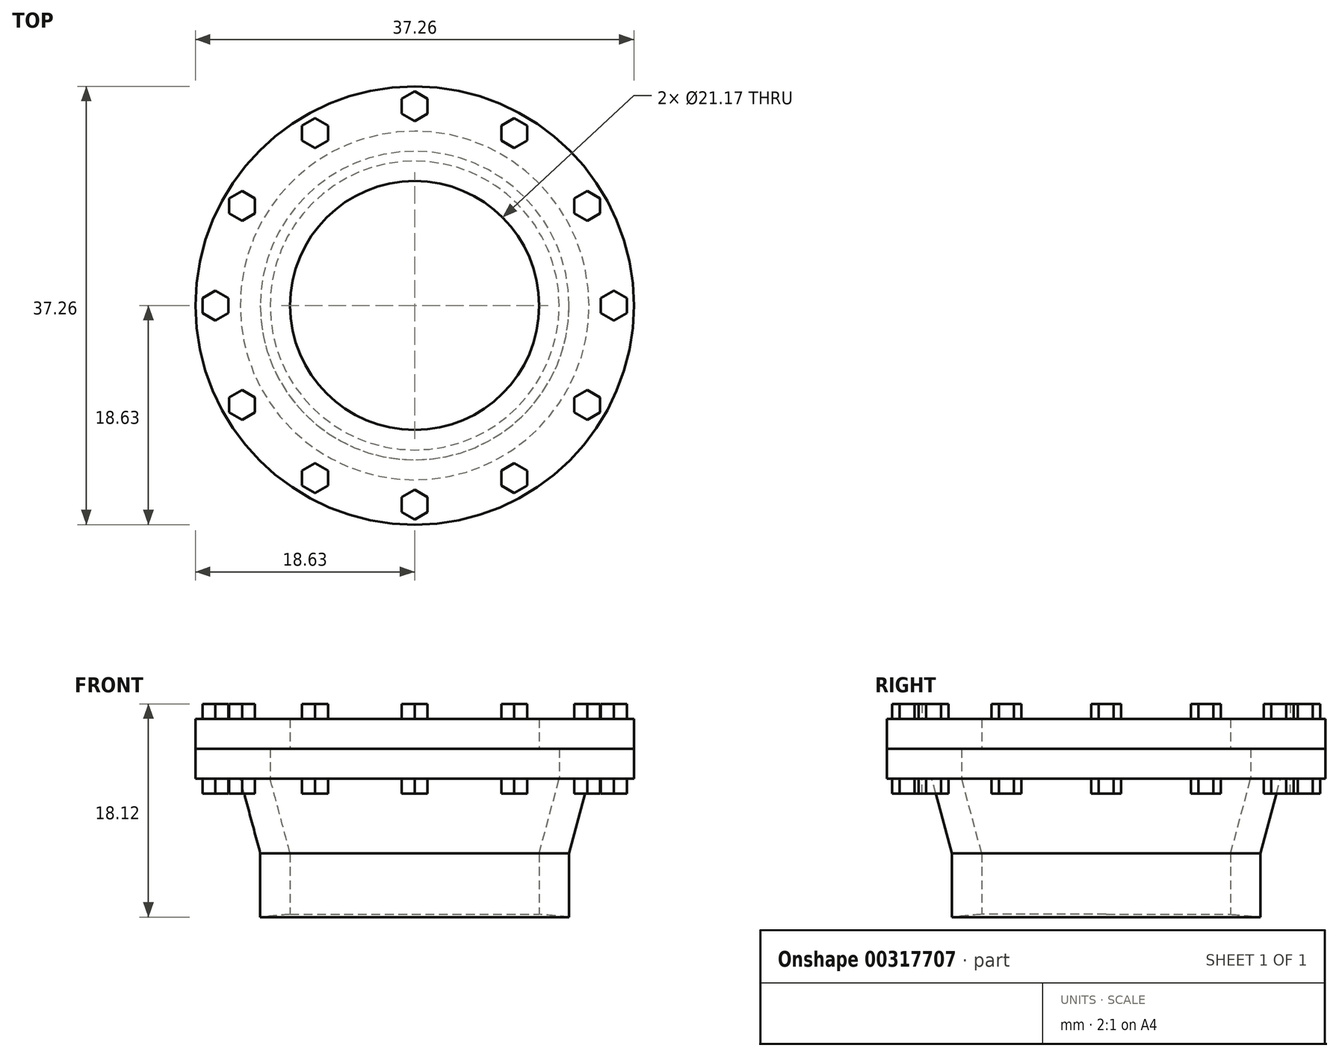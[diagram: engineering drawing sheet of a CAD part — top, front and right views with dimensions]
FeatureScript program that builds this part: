
annotation { "Feature Type Name" : "Feature", "Feature Type Description" : "" }
export const myFeature = defineFeature(function(context is Context, id is Id, definition is map)
    precondition{}
    {
        {
            var Q0;
            Q0=qCreatedBy(makeId("Front.planeOp"),FACE);
            var sketch = newSketch(context, id + "F0", { "sketchPlane" : qUnion([Q0])});
            skLineSegment(sketch, "E0", {"start": v(0, 0) * mm, "end": v(66.68, 0) * mm, "construction": true});
            skLineSegment(sketch, "E1", {"start": v(0, 0) * mm, "end": v(0, 33.34) * mm, "construction": true});
            skLineSegment(sketch, "E2", {"start": v(0, 33.34) * mm, "end": v(0, 36.51) * mm});
            skLineSegment(sketch, "E3", {"start": v(66.68, 0) * mm, "end": v(69.85, 0) * mm});
            skEllipse(sketch, "E4", {"center": v(0, 0) * mm, "majorRadius": 66.68 * mm, "minorRadius": 33.34 * mm, "majorAxis": v(1, 0)});
            skEllipse(sketch, "E5", {"center": v(0, 0) * mm, "majorRadius": 69.85 * mm, "minorRadius": 36.51 * mm, "majorAxis": v(1, 0)});
            skSolve(sketch);
        }
        {
            var Q0;
            {var subQ0=sQuery(id+"F0.wireOp",EDGE,"E2");Q0=makeQuery(id+"F0.imprint","IMPRINT",FACE,{"disambiguationData":[TD([[makeQuery(id+"F0.imprint","IMPRINT",EDGE,{"derivedFrom":subQ0}),-1.0]])]});}
            var Q1;
            Q1=sQuery(id+"F0.wireOp",EDGE,"E1");
            revolve(context, id + "F1", {"entities" : qUnion([Q0]), "axis" : qUnion([Q1]), "revolveType" : RevolveType.FULL});
        }
        {
            var Q0;
            Q0=qCreatedBy(makeId("Front.planeOp"),FACE);
            var sketch = newSketch(context, id + "F2", { "sketchPlane" : qUnion([Q0])});
            skLineSegment(sketch, "E6", {"start": v(0, 0) * mm, "end": v(0, 34.93) * mm, "construction": true});
            skLineSegment(sketch, "E7", {"start": v(-10.58, 34.93) * mm, "end": v(10.58, 34.93) * mm, "construction": true});
            skLineSegment(sketch, "E8", {"start": v(-10.58, 34.93) * mm, "end": v(-10.58, 33.02) * mm});
            skLineSegment(sketch, "E9", {"start": v(-10.58, 34.93) * mm, "end": v(-10.58, 41.27) * mm});
            skLineSegment(sketch, "E10", {"start": v(10.58, 34.93) * mm, "end": v(10.58, 33.02) * mm});
            skLineSegment(sketch, "E11", {"start": v(10.58, 34.93) * mm, "end": v(10.58, 41.27) * mm});
            skLineSegment(sketch, "E12.bottom", {"start": v(-10.58, 41.27) * mm, "end": v(-13.12, 41.27) * mm});
            skLineSegment(sketch, "E12.top", {"start": v(-10.58, 33.02) * mm, "end": v(-13.12, 33.02) * mm});
            skLineSegment(sketch, "E12.left", {"start": v(-10.58, 41.27) * mm, "end": v(-10.58, 33.02) * mm});
            skLineSegment(sketch, "E12.right", {"start": v(-13.12, 41.27) * mm, "end": v(-13.12, 33.02) * mm});
            skLineSegment(sketch, "E13", {"start": v(-13.12, 41.27) * mm, "end": v(-14.82, 47.62) * mm});
            skLineSegment(sketch, "E14", {"start": v(-14.82, 47.62) * mm, "end": v(-12.28, 47.62) * mm});
            skLineSegment(sketch, "E15", {"start": v(-12.28, 47.62) * mm, "end": v(-10.58, 41.27) * mm});
            skLineSegment(sketch, "E16.bottom", {"start": v(-12.28, 47.62) * mm, "end": v(-18.63, 47.62) * mm});
            skLineSegment(sketch, "E16.top", {"start": v(-12.28, 50.16) * mm, "end": v(-18.63, 50.16) * mm});
            skLineSegment(sketch, "E16.left", {"start": v(-12.28, 47.62) * mm, "end": v(-12.28, 50.17) * mm});
            skLineSegment(sketch, "E16.right", {"start": v(-18.63, 47.62) * mm, "end": v(-18.63, 50.16) * mm});
            skLineSegment(sketch, "E17", {"start": v(0, 34.93) * mm, "end": v(0, 57.33) * mm, "construction": true});
            skLineSegment(sketch, "E18.bottom", {"start": v(-12.28, 47.62) * mm, "end": v(0, 47.62) * mm});
            skLineSegment(sketch, "E18.top", {"start": v(-12.28, 50.17) * mm, "end": v(0, 50.17) * mm});
            skLineSegment(sketch, "E18.right", {"start": v(0, 47.62) * mm, "end": v(0, 50.17) * mm});
            skLineSegment(sketch, "E19.bottom", {"start": v(-18.63, 50.16) * mm, "end": v(0, 50.16) * mm});
            skLineSegment(sketch, "E19.top", {"start": v(-18.63, 52.7) * mm, "end": v(0, 52.7) * mm});
            skLineSegment(sketch, "E19.left", {"start": v(-18.63, 50.16) * mm, "end": v(-18.63, 52.7) * mm});
            skLineSegment(sketch, "E19.right", {"start": v(0, 50.17) * mm, "end": v(0, 52.7) * mm});
            skSolve(sketch);
        }
        {
            var Q0;
            Q0=makeQuery(id+"F2.imprint","IMPRINT",FACE,{"disambiguationData":[TD([[makeQuery(id+"F2.imprint","IMPRINT",EDGE,{"derivedFrom":sQuery(id+"F2.wireOp",EDGE,"E12.bottom")}),1.0]])]});
            var Q1;
            Q1=makeQuery(id+"F2.imprint","IMPRINT",FACE,{"disambiguationData":[TD([[makeQuery(id+"F2.imprint","IMPRINT",EDGE,{"derivedFrom":sQuery(id+"F2.wireOp",EDGE,"E12.bottom")}),-1.0]])]});
            var Q2;
            Q2=makeQuery(id+"F2.imprint","IMPRINT",FACE,{"disambiguationData":[TD([[makeQuery(id+"F2.imprint","IMPRINT",EDGE,{"derivedFrom":sQuery(id+"F2.wireOp",EDGE,"E16.top")}),1.0]])]});
            var Q3;
            {var subQ1=sQuery(id+"F2.wireOp",EDGE,"E16.right");Q3=makeQuery(id+"F2.imprint","IMPRINT",FACE,{"disambiguationData":[TD([[makeQuery(id+"F2.imprint","IMPRINT",EDGE,{"derivedFrom":subQ1}),-1.0]])]});}
            var Q4;
            Q4=sQuery(id+"F2.wireOp",EDGE,"E17");
            revolve(context, id + "F3", {"entities" : qUnion([Q0, Q1, Q2, Q3]), "axis" : qUnion([Q4]), "revolveType" : RevolveType.FULL});
        }
        {
            var Q0;
            Q0=makeQuery(id+"F2.imprint","IMPRINT",FACE,{"disambiguationData":[TD([[makeQuery(id+"F2.imprint","IMPRINT",EDGE,{"derivedFrom":sQuery(id+"F2.wireOp",EDGE,"E19.top")}),-1.0]])]});
            var Q1;
            Q1=sQuery(id+"F2.wireOp",EDGE,"E17");
            revolve(context, id + "F4", {"entities" : qUnion([Q0]), "axis" : qUnion([Q1]), "revolveType" : RevolveType.FULL});
        }
        {
            var Q0;
            Q0=makeQuery(id+"F4.opRevolve","SWEPT_FACE",FACE,{"disambiguationData":[OSD([sQuery(id+"F2.wireOp",EDGE,"E19.top")])]});
            var sketch = newSketch(context, id + "F5", { "sketchPlane" : qUnion([Q0])});
            skLineSegment(sketch, "E20", {"start": v(0, 0) * mm, "end": v(0, -16.93) * mm, "construction": true});
            skLineSegment(sketch, "E21", {"start": v(0, 0) * mm, "end": v(-16.93, 0) * mm, "construction": true});
            skLineSegment(sketch, "E22", {"start": v(0, 0) * mm, "end": v(0, 16.93) * mm, "construction": true});
            skLineSegment(sketch, "E23", {"start": v(0, 0) * mm, "end": v(16.93, 0) * mm, "construction": true});
            skLineSegment(sketch, "E24", {"start": v(0, 0) * mm, "end": v(8.47, 14.66) * mm, "construction": true});
            skLineSegment(sketch, "E25", {"start": v(0, 0) * mm, "end": v(14.66, 8.47) * mm, "construction": true});
            skLineSegment(sketch, "E26", {"start": v(0, 0) * mm, "end": v(14.66, -8.47) * mm, "construction": true});
            skLineSegment(sketch, "E27", {"start": v(0, 0) * mm, "end": v(8.47, -14.66) * mm, "construction": true});
            skLineSegment(sketch, "E28", {"start": v(0, 0) * mm, "end": v(-8.47, -14.66) * mm, "construction": true});
            skLineSegment(sketch, "E29", {"start": v(0, 0) * mm, "end": v(-14.66, -8.47) * mm, "construction": true});
            skLineSegment(sketch, "E30", {"start": v(0, 0) * mm, "end": v(-14.66, 8.47) * mm, "construction": true});
            skLineSegment(sketch, "E31", {"start": v(0, 0) * mm, "end": v(-8.47, 14.66) * mm, "construction": true});
            skCircle(sketch, "E32.cCircle", {"center": v(0, 16.93) * mm, "radius": 1.1 * mm, "construction": true});
            skLineSegment(sketch, "E32.0", {"start": v(1.1, 17.57) * mm, "end": v(1.1, 16.3) * mm});
            skLineSegment(sketch, "E32.1", {"start": v(1.1, 16.3) * mm, "end": v(0, 15.66) * mm});
            skLineSegment(sketch, "E32.2", {"start": v(0, 15.66) * mm, "end": v(-1.1, 16.3) * mm});
            skLineSegment(sketch, "E32.3", {"start": v(-1.1, 16.3) * mm, "end": v(-1.1, 17.57) * mm});
            skLineSegment(sketch, "E32.4", {"start": v(-1.1, 17.57) * mm, "end": v(0, 18.2) * mm});
            skLineSegment(sketch, "E32.5", {"start": v(0, 18.2) * mm, "end": v(1.1, 17.57) * mm});
            skPoint(sketch, "E32.0.midPoint", {"position": v(1.1, 16.93) * mm});
            skCircle(sketch, "E33.cCircle", {"center": v(8.47, 14.66) * mm, "radius": 1.1 * mm, "construction": true});
            skLineSegment(sketch, "E33.0", {"start": v(9.57, 15.3) * mm, "end": v(9.57, 14.03) * mm});
            skLineSegment(sketch, "E33.1", {"start": v(9.57, 14.03) * mm, "end": v(8.47, 13.4) * mm});
            skLineSegment(sketch, "E33.2", {"start": v(8.47, 13.4) * mm, "end": v(7.37, 14.03) * mm});
            skLineSegment(sketch, "E33.3", {"start": v(7.37, 14.03) * mm, "end": v(7.37, 15.3) * mm});
            skLineSegment(sketch, "E33.4", {"start": v(7.37, 15.3) * mm, "end": v(8.47, 15.93) * mm});
            skLineSegment(sketch, "E33.5", {"start": v(8.47, 15.93) * mm, "end": v(9.57, 15.3) * mm});
            skPoint(sketch, "E33.0.midPoint", {"position": v(9.57, 14.66) * mm});
            skCircle(sketch, "E34.cCircle", {"center": v(14.66, 8.47) * mm, "radius": 1.1 * mm, "construction": true});
            skLineSegment(sketch, "E34.0", {"start": v(15.76, 9.1) * mm, "end": v(15.76, 7.83) * mm});
            skLineSegment(sketch, "E34.1", {"start": v(15.76, 7.83) * mm, "end": v(14.66, 7.2) * mm});
            skLineSegment(sketch, "E34.2", {"start": v(14.66, 7.2) * mm, "end": v(13.56, 7.83) * mm});
            skLineSegment(sketch, "E34.3", {"start": v(13.56, 7.83) * mm, "end": v(13.56, 9.1) * mm});
            skLineSegment(sketch, "E34.4", {"start": v(13.56, 9.1) * mm, "end": v(14.66, 9.74) * mm});
            skLineSegment(sketch, "E34.5", {"start": v(14.66, 9.74) * mm, "end": v(15.76, 9.1) * mm});
            skPoint(sketch, "E34.0.midPoint", {"position": v(15.76, 8.47) * mm});
            skCircle(sketch, "E35.cCircle", {"center": v(16.93, 0) * mm, "radius": 1.1 * mm, "construction": true});
            skLineSegment(sketch, "E35.0", {"start": v(18.03, 0.64) * mm, "end": v(18.03, -0.64) * mm});
            skLineSegment(sketch, "E35.1", {"start": v(18.03, -0.64) * mm, "end": v(16.93, -1.27) * mm});
            skLineSegment(sketch, "E35.2", {"start": v(16.93, -1.27) * mm, "end": v(15.83, -0.64) * mm});
            skLineSegment(sketch, "E35.3", {"start": v(15.83, -0.64) * mm, "end": v(15.83, 0.64) * mm});
            skLineSegment(sketch, "E35.4", {"start": v(15.83, 0.64) * mm, "end": v(16.93, 1.27) * mm});
            skLineSegment(sketch, "E35.5", {"start": v(16.93, 1.27) * mm, "end": v(18.03, 0.64) * mm});
            skPoint(sketch, "E35.0.midPoint", {"position": v(18.03, 0) * mm});
            skCircle(sketch, "E36.cCircle", {"center": v(14.66, -8.47) * mm, "radius": 1.1 * mm, "construction": true});
            skLineSegment(sketch, "E36.0", {"start": v(15.76, -7.83) * mm, "end": v(15.76, -9.1) * mm});
            skLineSegment(sketch, "E36.1", {"start": v(15.76, -9.1) * mm, "end": v(14.66, -9.74) * mm});
            skLineSegment(sketch, "E36.2", {"start": v(14.66, -9.74) * mm, "end": v(13.56, -9.1) * mm});
            skLineSegment(sketch, "E36.3", {"start": v(13.56, -9.1) * mm, "end": v(13.56, -7.83) * mm});
            skLineSegment(sketch, "E36.4", {"start": v(13.56, -7.83) * mm, "end": v(14.66, -7.2) * mm});
            skLineSegment(sketch, "E36.5", {"start": v(14.66, -7.2) * mm, "end": v(15.76, -7.83) * mm});
            skPoint(sketch, "E36.0.midPoint", {"position": v(15.76, -8.47) * mm});
            skCircle(sketch, "E37.cCircle", {"center": v(8.47, -14.66) * mm, "radius": 1.1 * mm, "construction": true});
            skLineSegment(sketch, "E37.0", {"start": v(9.57, -14.03) * mm, "end": v(9.57, -15.3) * mm});
            skLineSegment(sketch, "E37.1", {"start": v(9.57, -15.3) * mm, "end": v(8.47, -15.93) * mm});
            skLineSegment(sketch, "E37.2", {"start": v(8.47, -15.93) * mm, "end": v(7.37, -15.3) * mm});
            skLineSegment(sketch, "E37.3", {"start": v(7.37, -15.3) * mm, "end": v(7.37, -14.03) * mm});
            skLineSegment(sketch, "E37.4", {"start": v(7.37, -14.03) * mm, "end": v(8.47, -13.4) * mm});
            skLineSegment(sketch, "E37.5", {"start": v(8.47, -13.4) * mm, "end": v(9.57, -14.03) * mm});
            skPoint(sketch, "E37.0.midPoint", {"position": v(9.57, -14.66) * mm});
            skCircle(sketch, "E38.cCircle", {"center": v(0, -16.93) * mm, "radius": 1.1 * mm, "construction": true});
            skLineSegment(sketch, "E38.0", {"start": v(1.1, -16.3) * mm, "end": v(1.1, -17.57) * mm});
            skLineSegment(sketch, "E38.1", {"start": v(1.1, -17.57) * mm, "end": v(0, -18.2) * mm});
            skLineSegment(sketch, "E38.2", {"start": v(0, -18.2) * mm, "end": v(-1.1, -17.57) * mm});
            skLineSegment(sketch, "E38.3", {"start": v(-1.1, -17.57) * mm, "end": v(-1.1, -16.3) * mm});
            skLineSegment(sketch, "E38.4", {"start": v(-1.1, -16.3) * mm, "end": v(0, -15.66) * mm});
            skLineSegment(sketch, "E38.5", {"start": v(0, -15.66) * mm, "end": v(1.1, -16.3) * mm});
            skPoint(sketch, "E38.0.midPoint", {"position": v(1.1, -16.93) * mm});
            skCircle(sketch, "E39.cCircle", {"center": v(-8.47, -14.66) * mm, "radius": 1.1 * mm, "construction": true});
            skLineSegment(sketch, "E39.0", {"start": v(-7.37, -14.03) * mm, "end": v(-7.37, -15.3) * mm});
            skLineSegment(sketch, "E39.1", {"start": v(-7.37, -15.3) * mm, "end": v(-8.47, -15.93) * mm});
            skLineSegment(sketch, "E39.2", {"start": v(-8.47, -15.93) * mm, "end": v(-9.57, -15.3) * mm});
            skLineSegment(sketch, "E39.3", {"start": v(-9.57, -15.3) * mm, "end": v(-9.57, -14.03) * mm});
            skLineSegment(sketch, "E39.4", {"start": v(-9.57, -14.03) * mm, "end": v(-8.47, -13.4) * mm});
            skLineSegment(sketch, "E39.5", {"start": v(-8.47, -13.4) * mm, "end": v(-7.37, -14.03) * mm});
            skPoint(sketch, "E39.0.midPoint", {"position": v(-7.37, -14.66) * mm});
            skCircle(sketch, "E40.cCircle", {"center": v(-14.66, -8.47) * mm, "radius": 1.1 * mm, "construction": true});
            skLineSegment(sketch, "E40.0", {"start": v(-13.56, -7.83) * mm, "end": v(-13.56, -9.1) * mm});
            skLineSegment(sketch, "E40.1", {"start": v(-13.56, -9.1) * mm, "end": v(-14.66, -9.74) * mm});
            skLineSegment(sketch, "E40.2", {"start": v(-14.66, -9.74) * mm, "end": v(-15.76, -9.1) * mm});
            skLineSegment(sketch, "E40.3", {"start": v(-15.76, -9.1) * mm, "end": v(-15.76, -7.83) * mm});
            skLineSegment(sketch, "E40.4", {"start": v(-15.76, -7.83) * mm, "end": v(-14.66, -7.2) * mm});
            skLineSegment(sketch, "E40.5", {"start": v(-14.66, -7.2) * mm, "end": v(-13.56, -7.83) * mm});
            skPoint(sketch, "E40.0.midPoint", {"position": v(-13.56, -8.47) * mm});
            skCircle(sketch, "E41.cCircle", {"center": v(-16.93, 0) * mm, "radius": 1.1 * mm, "construction": true});
            skLineSegment(sketch, "E41.0", {"start": v(-15.83, 0.64) * mm, "end": v(-15.83, -0.63) * mm});
            skLineSegment(sketch, "E41.1", {"start": v(-15.83, -0.63) * mm, "end": v(-16.93, -1.27) * mm});
            skLineSegment(sketch, "E41.2", {"start": v(-16.93, -1.27) * mm, "end": v(-18.03, -0.63) * mm});
            skLineSegment(sketch, "E41.3", {"start": v(-18.03, -0.63) * mm, "end": v(-18.03, 0.64) * mm});
            skLineSegment(sketch, "E41.4", {"start": v(-18.03, 0.63) * mm, "end": v(-16.93, 1.27) * mm});
            skLineSegment(sketch, "E41.5", {"start": v(-16.93, 1.27) * mm, "end": v(-15.83, 0.63) * mm});
            skPoint(sketch, "E41.0.midPoint", {"position": v(-15.83, 0) * mm});
            skCircle(sketch, "E42.cCircle", {"center": v(-14.66, 8.47) * mm, "radius": 1.1 * mm, "construction": true});
            skLineSegment(sketch, "E42.0", {"start": v(-13.56, 9.1) * mm, "end": v(-13.56, 7.83) * mm});
            skLineSegment(sketch, "E42.1", {"start": v(-13.56, 7.83) * mm, "end": v(-14.66, 7.2) * mm});
            skLineSegment(sketch, "E42.2", {"start": v(-14.66, 7.2) * mm, "end": v(-15.76, 7.83) * mm});
            skLineSegment(sketch, "E42.3", {"start": v(-15.76, 7.83) * mm, "end": v(-15.76, 9.1) * mm});
            skLineSegment(sketch, "E42.4", {"start": v(-15.76, 9.1) * mm, "end": v(-14.66, 9.74) * mm});
            skLineSegment(sketch, "E42.5", {"start": v(-14.66, 9.74) * mm, "end": v(-13.56, 9.1) * mm});
            skPoint(sketch, "E42.0.midPoint", {"position": v(-13.56, 8.47) * mm});
            skCircle(sketch, "E43.cCircle", {"center": v(-8.47, 14.66) * mm, "radius": 1.1 * mm, "construction": true});
            skLineSegment(sketch, "E43.0", {"start": v(-7.37, 15.3) * mm, "end": v(-7.37, 14.03) * mm});
            skLineSegment(sketch, "E43.1", {"start": v(-7.37, 14.03) * mm, "end": v(-8.47, 13.4) * mm});
            skLineSegment(sketch, "E43.2", {"start": v(-8.47, 13.4) * mm, "end": v(-9.57, 14.03) * mm});
            skLineSegment(sketch, "E43.3", {"start": v(-9.57, 14.03) * mm, "end": v(-9.57, 15.3) * mm});
            skLineSegment(sketch, "E43.4", {"start": v(-9.57, 15.3) * mm, "end": v(-8.47, 15.93) * mm});
            skLineSegment(sketch, "E43.5", {"start": v(-8.47, 15.93) * mm, "end": v(-7.37, 15.3) * mm});
            skPoint(sketch, "E43.0.midPoint", {"position": v(-7.37, 14.66) * mm});
            skSolve(sketch);
        }
        {
            var Q0;
            Q0 = qSketchRegion(id + "F5", true);
            extrude(context, id + "F6", {"entities" : qUnion([Q0]), "operationType" : NewBodyOperationType.ADD, "depth" : 1.27 * mm, "offsetDistance" : 25.4 * mm});
        }
        {
            var Q0;
            Q0 = qSketchRegion(id + "F5", true);
            extrude(context, id + "F7", {"entities" : qUnion([Q0]), "operationType" : NewBodyOperationType.ADD, "oppositeDirection" : true, "depth" : 6.35 * mm, "offsetDistance" : 25.4 * mm, "hasSecondDirection" : true, "secondDirectionOppositeDirection" : true, "secondDirectionDepth" : 5.08 * mm});
        }
        {
            var Q0;
            {var subQ0=sQuery(id+"F0.wireOp",EDGE,"E2");Q0=makeQuery(id+"F0.imprint","IMPRINT",FACE,{"disambiguationData":[TD([[makeQuery(id+"F0.imprint","IMPRINT",EDGE,{"derivedFrom":subQ0}),-1.0]])]});}
            var Q1;
            Q1=sQuery(id+"F0.wireOp",EDGE,"E1");
            revolve(context, id + "F8", {"operationType" : NewBodyOperationType.REMOVE, "entities" : qUnion([Q0]), "axis" : qUnion([Q1]), "revolveType" : RevolveType.FULL, "oppositeDirection" : true});
        }
        {
            var Q0;
            Q0=qCreatedBy(makeId("Top.planeOp"),FACE);
            var sketch = newSketch(context, id + "F9", { "sketchPlane" : qUnion([Q0])});
            skCircle(sketch, "E44", {"center": v(0, 0) * mm, "radius": 10.58 * mm});
            skSolve(sketch);
        }
        {
            var Q0;
            Q0 = qSketchRegion(id + "F9", true);
            extrude(context, id + "F10", {"entities" : qUnion([Q0]), "operationType" : NewBodyOperationType.REMOVE, "depth" : 254 * mm, "offsetDistance" : 25.4 * mm});
        }
    });
